# Revit family: РИДАН_082X6113RL-082X6113RL2 - C101-R DN125 PN16
name_source: partatom
category: Арматура трубопроводов
units: mm (PartAtom-declared; Revit-internal decimal feet)

## family parameters
Всегда вертикально = Да
На основе рабочей плоскости = Нет
Общий = Нет
При загрузке вырезать с полостями = Нет
Размер круглого соединителя = Использовать диаметр
Тип детали = Вставляется

## types (2) — shared parameters
ADSK_Версия Revit = 2019
ADSK_Версия семейства = 1.0
ADSK_Диаметр условный = 125 мм
ADSK_Единица измерения = шт.
ADSK_Завод-изготовитель = ООО «Ридан-Трейд»
ADSK_Количество = 1
ADSK_Марка = С101-R DN125
ADSK_Масса = 1
ADSK_Потеря давления жидкости = 0.0 Па
ADSK_Пропускная способность = 350 м³/ч
ADSK_Расход жидкости = 0 м³/ч
URL = https://ridan.ru
Изготовитель = ООО «Ридан-Трейд»

## per-type parameters (varying)
| type | ADSK_Код изделия | ADSK_Наименование |
| DN125, PN25, 1-8 бар | 082X6113RL | Регулятор давления «после себя» С101-R PN25, 1-8 бар, DN125 |
| DN125, PN25, 2-16 бар | 082X6113RL2 | Регулятор давления «после себя» С101-R PN25, 2-16 бар, DN125 |
